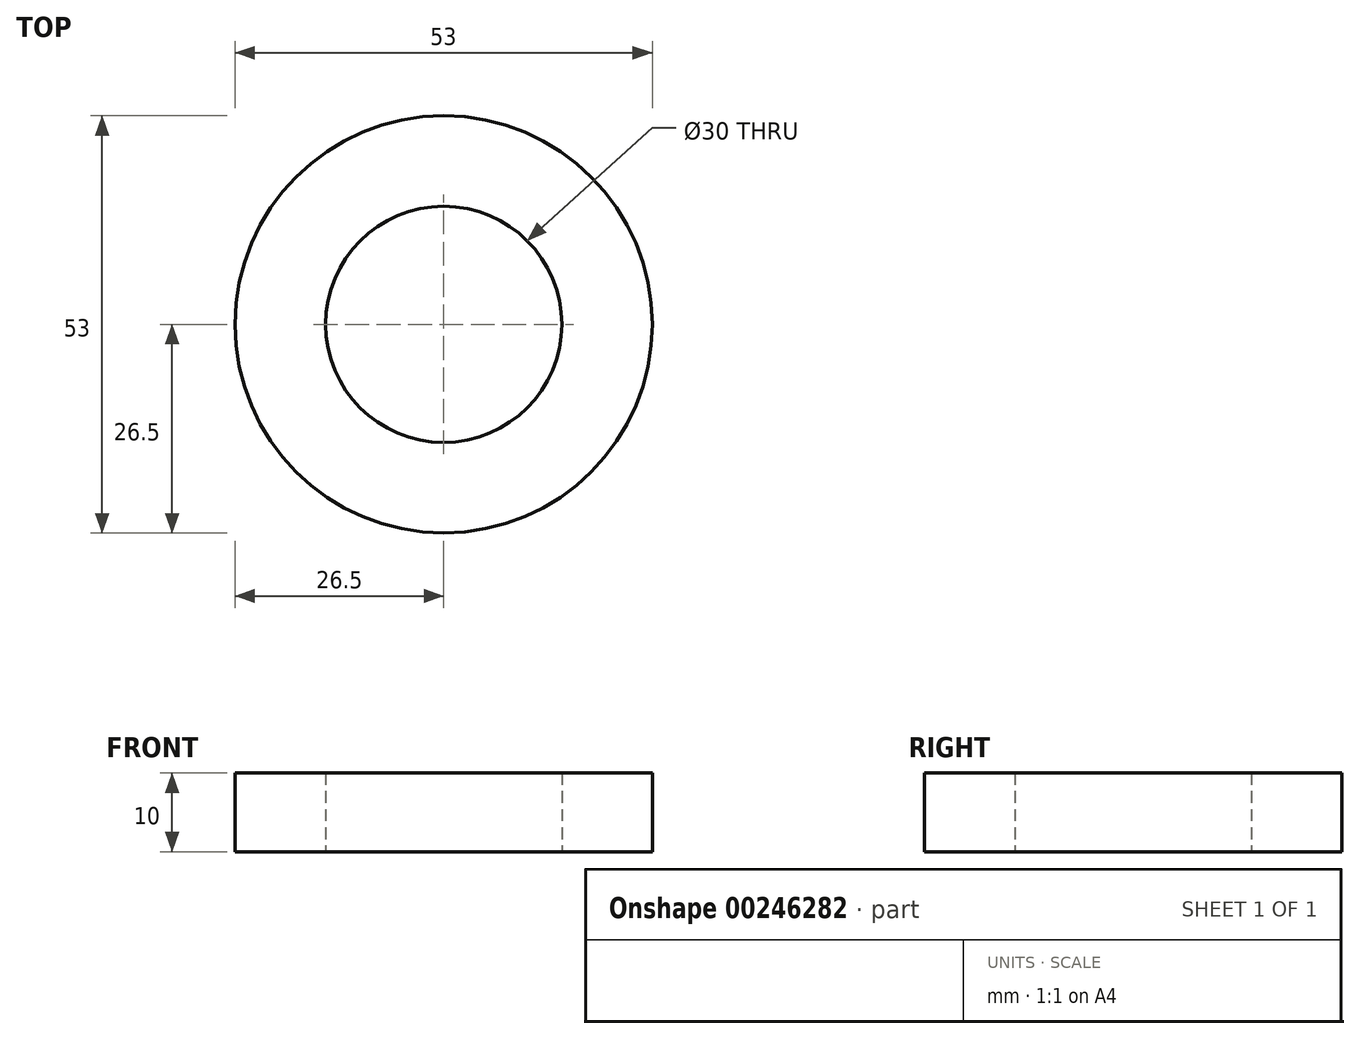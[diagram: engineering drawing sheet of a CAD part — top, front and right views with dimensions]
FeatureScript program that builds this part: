
annotation { "Feature Type Name" : "Feature", "Feature Type Description" : "" }
export const myFeature = defineFeature(function(context is Context, id is Id, definition is map)
    precondition{}
    {
        {
            var Q0;
            Q0=qCreatedBy(makeId("Top.planeOp"),FACE);
            var sketch = newSketch(context, id + "F0", { "sketchPlane" : qUnion([Q0])});
            skCircle(sketch, "E0", {"center": v(0, 0) * mm, "radius": 15 * mm});
            skCircle(sketch, "E1", {"center": v(0, 0) * mm, "radius": 26.5 * mm});
            skSolve(sketch);
        }
        {
            var Q0;
            Q0 = qSketchRegion(id + "F0", true);
            extrude(context, id + "F1", {"entities" : qUnion([Q0]), "depth" : 10 * mm});
        }
    });
